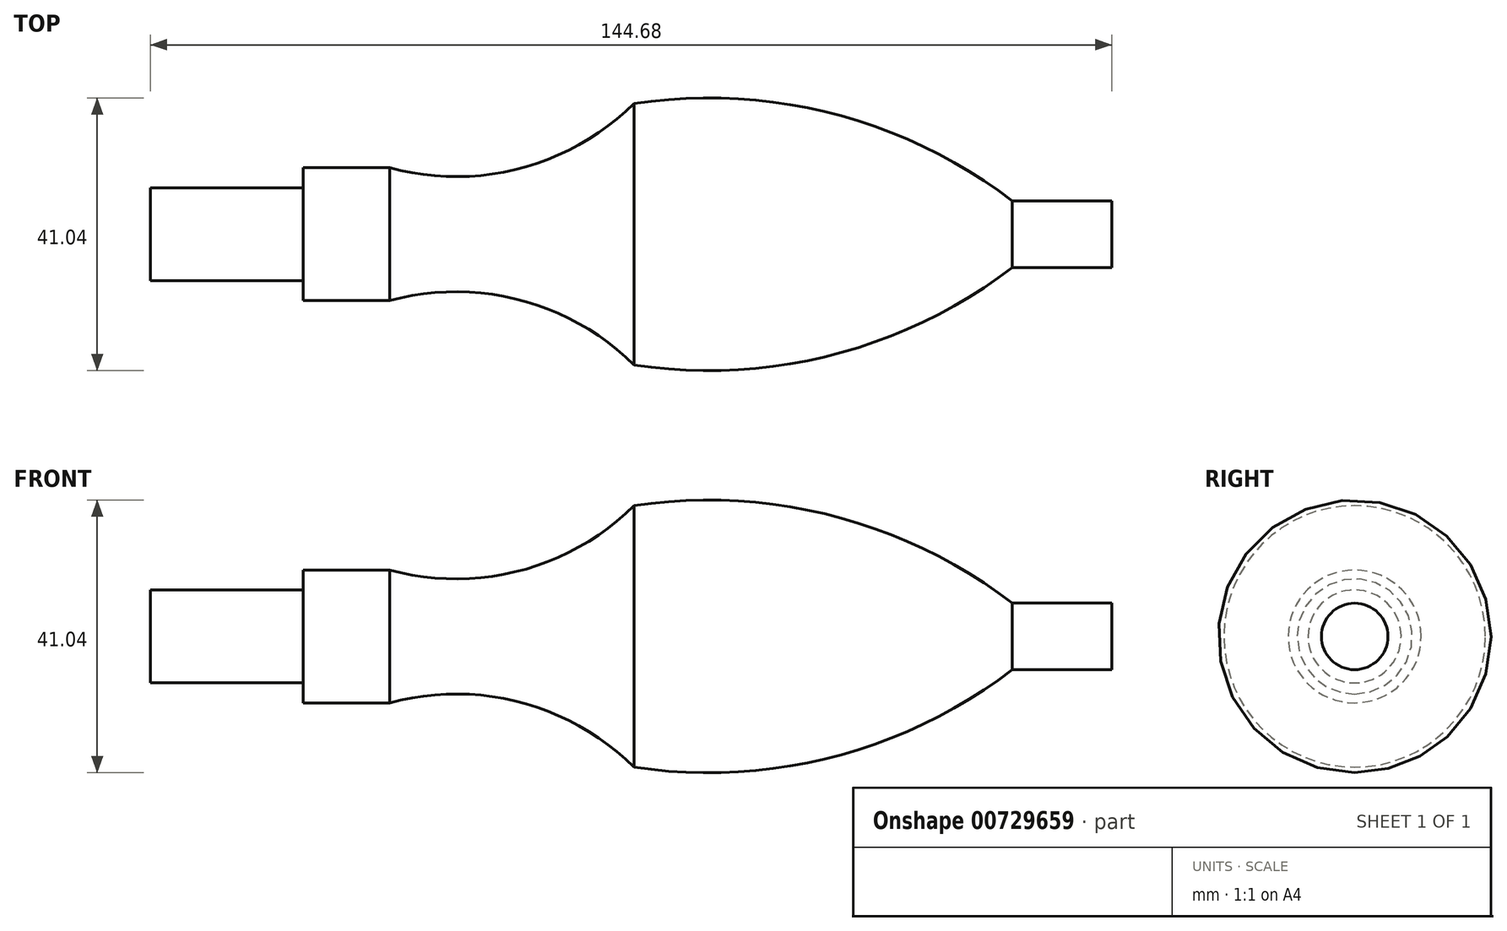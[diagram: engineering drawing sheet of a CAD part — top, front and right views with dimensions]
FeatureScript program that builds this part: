
annotation { "Feature Type Name" : "Feature", "Feature Type Description" : "" }
export const myFeature = defineFeature(function(context is Context, id is Id, definition is map)
    precondition{}
    {
        {
            var Q0;
            Q0=qCreatedBy(makeId("Top.planeOp"),FACE);
            var sketch = newSketch(context, id + "F0", { "sketchPlane" : qUnion([Q0])});
            skLineSegment(sketch, "E0", {"start": v(0, 0) * mm, "end": v(29, 0) * mm, "construction": true});
            skLineSegment(sketch, "E1", {"start": v(0, 0) * mm, "end": v(-38, 0) * mm, "construction": true});
            skLineSegment(sketch, "E2", {"start": v(-38, 0) * mm, "end": v(-61, 0) * mm, "construction": true});
            skLineSegment(sketch, "E3", {"start": v(-61, -7) * mm, "end": v(-61, -10) * mm});
            skLineSegment(sketch, "E4", {"start": v(-61, -10) * mm, "end": v(-48, -10) * mm});
            skLineSegment(sketch, "E5.top", {"start": v(-84, -7) * mm, "end": v(-61, -7) * mm});
            skLineSegment(sketch, "E6.top", {"start": v(60.68, -5) * mm, "end": v(45.68, -5) * mm});
            skLineSegment(sketch, "E6.left", {"start": v(60.68, 0) * mm, "end": v(60.68, -5) * mm});
            skLineSegment(sketch, "E7", {"start": v(60.68, 0) * mm, "end": v(-84, 0) * mm});
            skLineSegment(sketch, "E8.trimOffspring", {"start": v(-84, 0) * mm, "end": v(-84, -7) * mm});
            skPoint(sketch, "E9.orphan", {"position": v(-84, 7) * mm});
            skArc(sketch, "E10.trimOffspring", {"start": v(-11.25, -19.67) * mm, "mid": v(18.71, -18.15) * mm, "end": v(45.68, -5) * mm});
            skArc(sketch, "E11.trimOffspring", {"start": v(-11.25, -19.67) * mm, "mid": v(-28.33, -9.91) * mm, "end": v(-48, -10) * mm});
            skPoint(sketch, "E6.bottom.start.orphan", {"position": v(60.68, 5) * mm});
            skSolve(sketch);
        }
        {
            var Q0;
            Q0=makeQuery(id+"F0.imprint","IMPRINT",FACE,{"disambiguationData":[TD([[makeQuery(id+"F0.imprint","IMPRINT",EDGE,{"derivedFrom":sQuery(id+"F0.wireOp",EDGE,"E3")}),1.0]])]});
            var Q1;
            Q1=sQuery(id+"F0.wireOp",EDGE,"E7");
            revolve(context, id + "F1", {"surfaceOperationType" : NewSurfaceOperationType.NEW, "entities" : qUnion([Q0]), "axis" : qUnion([Q1]), "revolveType" : RevolveType.FULL});
        }
    });
